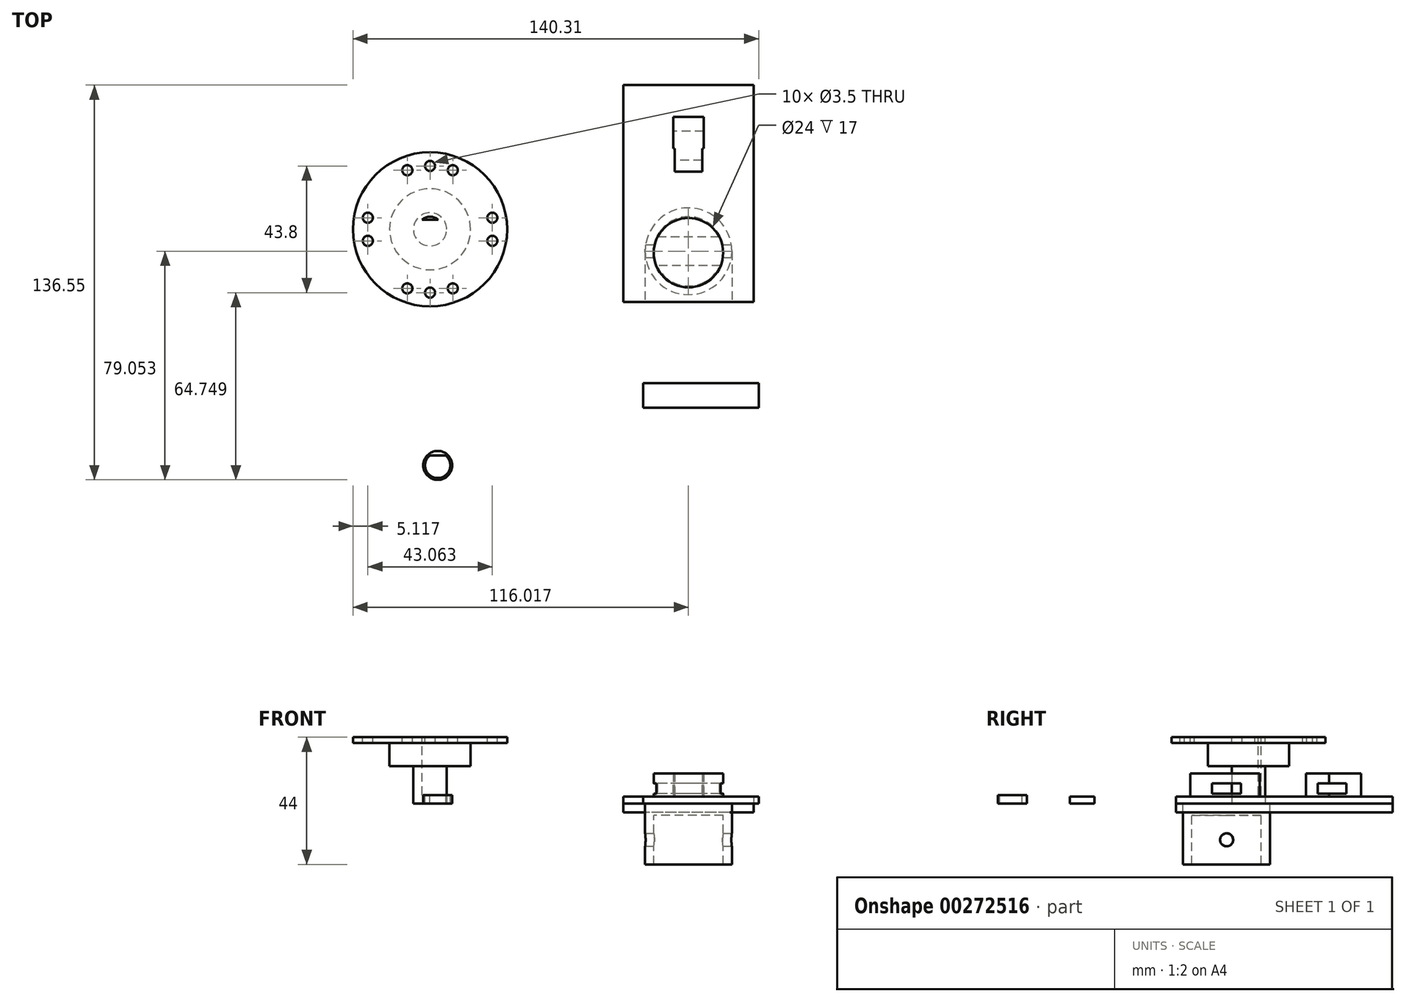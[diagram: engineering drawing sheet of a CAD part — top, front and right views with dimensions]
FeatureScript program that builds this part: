
annotation { "Feature Type Name" : "Feature", "Feature Type Description" : "" }
export const myFeature = defineFeature(function(context is Context, id is Id, definition is map)
    precondition{}
    {
        {
            var Q0;
            Q0=qCreatedBy(makeId("Top.planeOp"),FACE);
            var sketch = newSketch(context, id + "F0", { "sketchPlane" : qUnion([Q0])});
            skLineSegment(sketch, "E0.bottom", {"start": v(64.4, 9.3) * mm, "end": v(19.4, 9.3) * mm});
            skLineSegment(sketch, "E0.top", {"start": v(64.4, 84.3) * mm, "end": v(19.4, 84.3) * mm});
            skLineSegment(sketch, "E0.left", {"start": v(64.4, 9.3) * mm, "end": v(64.4, 84.3) * mm});
            skLineSegment(sketch, "E0.right", {"start": v(19.4, 9.3) * mm, "end": v(19.4, 84.3) * mm});
            skPoint(sketch, "E0.middle", {"position": v(41.9, 46.8) * mm});
            skSolve(sketch);
        }
        {
            var Q0;
            Q0=makeQuery(id+"F0.imprint","IMPRINT",FACE,{"disambiguationData":[TD([[makeQuery(id+"F0.imprint","IMPRINT",EDGE,{"derivedFrom":sQuery(id+"F0.wireOp",EDGE,"E0.bottom")}),-1.0]])]});
            extrude(context, id + "F1", {"entities" : qUnion([Q0]), "depth" : 2.5 * mm});
        }
        {
            var Q0;
            Q0=makeQuery(id+"F1.opExtrude","CAP_FACE",FACE,{"disambiguationData":[OSD([sQuery(id+"F0.wireOp",EDGE,"E0.bottom"),sQuery(id+"F0.wireOp",EDGE,"E0.top"),sQuery(id+"F0.wireOp",EDGE,"E0.left"),sQuery(id+"F0.wireOp",EDGE,"E0.right")])],"isStart":false});
            var sketch = newSketch(context, id + "F2", { "sketchPlane" : qUnion([Q0])});
            skCircle(sketch, "E1", {"center": v(41.9, 26.3) * mm, "radius": 12 * mm});
            skPoint(sketch, "E1.centerSnap0", {"position": v(41.9, 9.3) * mm});
            skPoint(sketch, "E2", {"position": v(41.9, 38.3) * mm});
            skLineSegment(sketch, "E3.bottom", {"start": v(46.65, 54.3) * mm, "end": v(37.15, 54.3) * mm});
            skLineSegment(sketch, "E3.top", {"start": v(46.65, 62.3) * mm, "end": v(37.15, 62.3) * mm});
            skLineSegment(sketch, "E3.left", {"start": v(46.65, 54.3) * mm, "end": v(46.65, 62.3) * mm});
            skLineSegment(sketch, "E3.right", {"start": v(37.15, 54.3) * mm, "end": v(37.15, 62.3) * mm});
            skPoint(sketch, "E3.middle", {"position": v(41.9, 58.3) * mm});
            skPoint(sketch, "E4", {"position": v(41.9, 54.3) * mm});
            skLineSegment(sketch, "E5.bottom", {"start": v(36.65, 62.3) * mm, "end": v(47.15, 62.3) * mm});
            skLineSegment(sketch, "E5.top", {"start": v(36.65, 73.3) * mm, "end": v(47.15, 73.3) * mm});
            skLineSegment(sketch, "E5.left", {"start": v(36.65, 62.3) * mm, "end": v(36.65, 73.3) * mm});
            skLineSegment(sketch, "E5.right", {"start": v(47.15, 62.3) * mm, "end": v(47.15, 73.3) * mm});
            skSolve(sketch);
        }
        {
            var Q0;
            Q0 = qSketchRegion(id + "F2", true);
            extrude(context, id + "F3", {"entities" : qUnion([Q0]), "operationType" : NewBodyOperationType.ADD, "depth" : 8 * mm});
        }
        {
            var Q0;
            Q0=makeQuery(id+"F0.imprint","IMPRINT",FACE,{"disambiguationData":[TD([[makeQuery(id+"F0.imprint","IMPRINT",EDGE,{"derivedFrom":sQuery(id+"F0.wireOp",EDGE,"E0.bottom")}),-1.0]])]});
            var sketch = newSketch(context, id + "F4", { "sketchPlane" : qUnion([Q0])});
            skPoint(sketch, "E6", {"position": v(41.9, 84.2) * mm});
            skPoint(sketch, "E7", {"position": v(41.9, 46.86) * mm});
            skLineSegment(sketch, "E8", {"start": v(41.9, 46.86) * mm, "end": v(41.9, 84.2) * mm});
            skCircle(sketch, "E9", {"center": v(41.9, 26.8) * mm, "radius": 15 * mm});
            skCircle(sketch, "E10", {"center": v(41.9, 26.8) * mm, "radius": 12 * mm});
            skSolve(sketch);
        }
        {
            var Q0;
            Q0=makeQuery(id+"F4.imprint","IMPRINT",FACE,{"disambiguationData":[TD([[makeQuery(id+"F4.imprint","IMPRINT",EDGE,{"derivedFrom":sQuery(id+"F4.wireOp",EDGE,"E9")}),1.0]])]});
            var Q1;
            Q1=makeQuery(id+"F4.imprint","IMPRINT",FACE,{"disambiguationData":[TD([[makeQuery(id+"F4.imprint","IMPRINT",EDGE,{"derivedFrom":sQuery(id+"F4.wireOp",EDGE,"E10")}),1.0]])]});
            extrude(context, id + "F5", {"entities" : qUnion([Q0, Q1]), "operationType" : NewBodyOperationType.ADD, "oppositeDirection" : true, "depth" : 4 * mm});
        }
        {
            var Q0;
            Q0 = qSketchRegion(id + "F4", true);
            extrude(context, id + "F6", {"entities" : qUnion([Q0]), "operationType" : NewBodyOperationType.ADD, "oppositeDirection" : true, "depth" : 21 * mm});
        }
        {
            var Q0;
            Q0=makeQuery(id+"F1.opExtrude","SWEPT_FACE",FACE,{"disambiguationData":[OSD([sQuery(id+"F0.wireOp",EDGE,"E0.bottom")])]});
            var sketch = newSketch(context, id + "F7", { "sketchPlane" : qUnion([Q0])});
            skLineSegment(sketch, "E11.bottom", {"start": v(62.65, -17.52) * mm, "end": v(21.14, -17.52) * mm});
            skLineSegment(sketch, "E11.top", {"start": v(62.65, 20.02) * mm, "end": v(21.14, 20.02) * mm});
            skLineSegment(sketch, "E11.left", {"start": v(62.65, -17.52) * mm, "end": v(62.65, 20.02) * mm});
            skLineSegment(sketch, "E11.right", {"start": v(21.14, -17.52) * mm, "end": v(21.14, 20.02) * mm});
            skPoint(sketch, "E11.middle", {"position": v(41.9, 1.25) * mm});
            skPoint(sketch, "E11.middle.positionSnap0", {"position": v(64.4, 1.25) * mm});
            skPoint(sketch, "E11.middle.positionSnap1", {"position": v(41.9, 2.5) * mm});
            skPoint(sketch, "E11.centerSnap0", {"position": v(64.4, 1.25) * mm});
            skPoint(sketch, "E11.centerSnap1", {"position": v(41.9, 2.5) * mm});
            skSolve(sketch);
        }
        {
            var Q0;
            Q0 = qSketchRegion(id + "F7", true);
            extrude(context, id + "F8", {"entities" : qUnion([Q0]), "operationType" : NewBodyOperationType.ADD, "depth" : 1 * mm});
        }
        {
            var Q0;
            Q0=makeQuery(id+"F8.opExtrude","CAP_FACE",FACE,{"disambiguationData":[OSD([sQuery(id+"F7.wireOp",EDGE,"E11.bottom"),sQuery(id+"F7.wireOp",EDGE,"E11.top"),sQuery(id+"F7.wireOp",EDGE,"E11.left"),sQuery(id+"F7.wireOp",EDGE,"E11.right")])],"isStart":false});
            var sketch = newSketch(context, id + "F9", { "sketchPlane" : qUnion([Q0])});
            skLineSegment(sketch, "E12.bottom", {"start": v(21.14, 20.02) * mm, "end": v(62.65, 20.02) * mm});
            skLineSegment(sketch, "E12.top", {"start": v(21.14, -17.52) * mm, "end": v(62.65, -17.52) * mm});
            skLineSegment(sketch, "E12.left", {"start": v(21.14, 20.02) * mm, "end": v(21.14, -17.52) * mm});
            skLineSegment(sketch, "E12.right", {"start": v(62.65, 20.02) * mm, "end": v(62.65, -17.52) * mm});
            skSolve(sketch);
        }
        {
            var Q0;
            Q0 = qSketchRegion(id + "F9", true);
            extrude(context, id + "F10", {"entities" : qUnion([Q0]), "operationType" : NewBodyOperationType.REMOVE, "oppositeDirection" : true, "depth" : 1 * mm});
        }
        {
            var Q0;
            Q0=makeQuery(id+"F1.opExtrude","SWEPT_FACE",FACE,{"disambiguationData":[OSD([sQuery(id+"F0.wireOp",EDGE,"E0.right")])]});
            var sketch = newSketch(context, id + "F11", { "sketchPlane" : qUnion([Q0])});
            skLineSegment(sketch, "E13.bottom", {"start": v(-84.3, 0) * mm, "end": v(-9.3, 0) * mm});
            skLineSegment(sketch, "E13.top", {"start": v(-84.3, 7.62) * mm, "end": v(-9.3, 7.62) * mm});
            skLineSegment(sketch, "E13.left", {"start": v(-84.3, 0) * mm, "end": v(-84.3, 7.62) * mm});
            skLineSegment(sketch, "E13.right", {"start": v(-9.3, 0) * mm, "end": v(-9.3, 7.62) * mm});
            skSolve(sketch);
        }
        {
            var Q0;
            Q0 = qSketchRegion(id + "F11", true);
            extrude(context, id + "F12", {"entities" : qUnion([Q0]), "operationType" : NewBodyOperationType.ADD, "depth" : 1 * mm});
        }
        {
            var Q0;
            Q0=makeQuery(id+"F12.opExtrude","CAP_FACE",FACE,{"disambiguationData":[OSD([sQuery(id+"F11.wireOp",EDGE,"E13.bottom"),sQuery(id+"F11.wireOp",EDGE,"E13.top"),sQuery(id+"F11.wireOp",EDGE,"E13.left"),sQuery(id+"F11.wireOp",EDGE,"E13.right")])],"isStart":false});
            var sketch = newSketch(context, id + "F13", { "sketchPlane" : qUnion([Q0])});
            skPoint(sketch, "E14", {"position": v(-26.8, 3.5) * mm});
            skLineSegment(sketch, "E15.bottom", {"start": v(-31.8, 3.5) * mm, "end": v(-21.8, 3.5) * mm});
            skLineSegment(sketch, "E15.top", {"start": v(-31.8, 7) * mm, "end": v(-21.8, 7) * mm});
            skLineSegment(sketch, "E15.left", {"start": v(-31.8, 3.5) * mm, "end": v(-31.8, 7) * mm});
            skLineSegment(sketch, "E15.right", {"start": v(-21.8, 3.5) * mm, "end": v(-21.8, 7) * mm});
            skLineSegment(sketch, "E16.bottom", {"start": v(-58.3, 3.5) * mm, "end": v(-68.3, 3.5) * mm});
            skLineSegment(sketch, "E16.top", {"start": v(-58.3, 7) * mm, "end": v(-68.3, 7) * mm});
            skLineSegment(sketch, "E16.left", {"start": v(-58.3, 3.5) * mm, "end": v(-58.3, 7) * mm});
            skLineSegment(sketch, "E16.right", {"start": v(-68.3, 3.5) * mm, "end": v(-68.3, 7) * mm});
            skPoint(sketch, "E17", {"position": v(-63.3, 5.25) * mm});
            skPoint(sketch, "E17.positionSnap0", {"position": v(-58.3, 5.25) * mm});
            skPoint(sketch, "E17.positionSnap1", {"position": v(-63.3, 3.5) * mm});
            skSolve(sketch);
        }
        {
            var Q0;
            Q0=makeQuery(id+"F13.imprint","IMPRINT",FACE,{"disambiguationData":[TD([[makeQuery(id+"F13.imprint","IMPRINT",EDGE,{"derivedFrom":sQuery(id+"F13.wireOp",EDGE,"E16.bottom")}),-1.0]])]});
            var Q1;
            Q1=makeQuery(id+"F13.imprint","IMPRINT",FACE,{"disambiguationData":[TD([[makeQuery(id+"F13.imprint","IMPRINT",EDGE,{"derivedFrom":sQuery(id+"F13.wireOp",EDGE,"E15.bottom")}),1.0]])]});
            extrude(context, id + "F14", {"entities" : qUnion([Q0, Q1]), "operationType" : NewBodyOperationType.REMOVE, "endBound" : BoundingType.THROUGH_ALL, "oppositeDirection" : true, "depth" : 25 * mm});
        }
        {
            var Q0;
            Q0=makeQuery(id+"F12.opExtrude","CAP_FACE",FACE,{"disambiguationData":[OSD([sQuery(id+"F11.wireOp",EDGE,"E13.bottom"),sQuery(id+"F11.wireOp",EDGE,"E13.top"),sQuery(id+"F11.wireOp",EDGE,"E13.left"),sQuery(id+"F11.wireOp",EDGE,"E13.right")])],"isStart":false});
            var sketch = newSketch(context, id + "F15", { "sketchPlane" : qUnion([Q0])});
            skLineSegment(sketch, "E18.bottom", {"start": v(-84.3, 7.62) * mm, "end": v(-9.3, 7.62) * mm});
            skLineSegment(sketch, "E18.top", {"start": v(-84.3, 0) * mm, "end": v(-9.3, 0) * mm});
            skLineSegment(sketch, "E18.left", {"start": v(-84.3, 7.62) * mm, "end": v(-84.3, 0) * mm});
            skLineSegment(sketch, "E18.right", {"start": v(-9.3, 7.62) * mm, "end": v(-9.3, 0) * mm});
            skSolve(sketch);
        }
        {
            var Q0;
            Q0 = qSketchRegion(id + "F15", true);
            extrude(context, id + "F16", {"entities" : qUnion([Q0]), "operationType" : NewBodyOperationType.REMOVE, "oppositeDirection" : true, "depth" : 1 * mm});
        }
        {
            var Q0;
            Q0=qCreatedBy(makeId("Top.planeOp"),FACE);
            var sketch = newSketch(context, id + "F17", { "sketchPlane" : qUnion([Q0])});
            skCircle(sketch, "E19", {"center": v(-47.47, 34.39) * mm, "radius": 5.75 * mm});
            skSolve(sketch);
        }
        {
            var Q0;
            Q0 = qSketchRegion(id + "F17", true);
            extrude(context, id + "F18", {"entities" : qUnion([Q0]), "depth" : 13 * mm});
        }
        {
            var Q0;
            Q0=makeQuery(id+"F18.opExtrude","CAP_FACE",FACE,{"disambiguationData":[OSD([sQuery(id+"F17.wireOp",EDGE,"E19")])],"isStart":false});
            var sketch = newSketch(context, id + "F19", { "sketchPlane" : qUnion([Q0])});
            skCircle(sketch, "E20", {"center": v(-47.47, 34.39) * mm, "radius": 14 * mm});
            skSolve(sketch);
        }
        {
            var Q0;
            Q0 = qSketchRegion(id + "F19", true);
            extrude(context, id + "F20", {"entities" : qUnion([Q0]), "operationType" : NewBodyOperationType.ADD, "depth" : 8 * mm});
        }
        {
            var Q0;
            Q0=makeQuery(id+"F20.opExtrude","CAP_FACE",FACE,{"disambiguationData":[OSD([sQuery(id+"F19.wireOp",EDGE,"E20")])],"isStart":false});
            var sketch = newSketch(context, id + "F21", { "sketchPlane" : qUnion([Q0])});
            skCircle(sketch, "E21", {"center": v(-47.47, 34.39) * mm, "radius": 26.65 * mm});
            skSolve(sketch);
        }
        {
            var Q0;
            Q0 = qSketchRegion(id + "F21", true);
            extrude(context, id + "F22", {"entities" : qUnion([Q0]), "operationType" : NewBodyOperationType.ADD, "depth" : 2 * mm});
        }
        {
            var Q0;
            Q0=makeQuery(id+"F22.opExtrude","CAP_FACE",FACE,{"disambiguationData":[OSD([sQuery(id+"F21.wireOp",EDGE,"E21")])],"isStart":false});
            var sketch = newSketch(context, id + "F23", { "sketchPlane" : qUnion([Q0])});
            skPoint(sketch, "E22", {"position": v(-47.47, 34.39) * mm});
            skPoint(sketch, "E23", {"position": v(-47.47, 61.04) * mm});
            skPoint(sketch, "E24", {"position": v(-47.47, 7.74) * mm});
            skPoint(sketch, "E25", {"position": v(-20.82, 34.39) * mm});
            skPoint(sketch, "E26", {"position": v(-74.12, 34.39) * mm});
            skCircle(sketch, "E27", {"center": v(-47.47, 56.29) * mm, "radius": 1.75 * mm});
            skCircle(sketch, "E28", {"center": v(-47.47, 12.49) * mm, "radius": 1.75 * mm});
            skCircle(sketch, "E29", {"center": v(-25.94, 38.39) * mm, "radius": 1.75 * mm});
            skCircle(sketch, "E30", {"center": v(-25.94, 30.39) * mm, "radius": 1.75 * mm});
            skCircle(sketch, "E31", {"center": v(-69, 30.39) * mm, "radius": 1.75 * mm});
            skCircle(sketch, "E32", {"center": v(-69, 38.39) * mm, "radius": 1.75 * mm});
            skPoint(sketch, "E33", {"position": v(-25.82, 34.39) * mm});
            skPoint(sketch, "E34", {"position": v(-69.12, 34.39) * mm});
            skCircle(sketch, "E35", {"center": v(-39.6, 54.83) * mm, "radius": 1.75 * mm});
            skCircle(sketch, "E36", {"center": v(-55.34, 54.83) * mm, "radius": 1.75 * mm});
            skCircle(sketch, "E37", {"center": v(-39.6, 13.95) * mm, "radius": 1.75 * mm});
            skCircle(sketch, "E38", {"center": v(-55.34, 13.95) * mm, "radius": 1.75 * mm});
            skSolve(sketch);
        }
        {
            var Q0;
            Q0 = qSketchRegion(id + "F23", true);
            extrude(context, id + "F24", {"entities" : qUnion([Q0]), "operationType" : NewBodyOperationType.REMOVE, "oppositeDirection" : true, "depth" : 25 * mm});
        }
        {
            var Q0;
            Q0=makeQuery(id+"F22.opExtrude","CAP_FACE",FACE,{"disambiguationData":[OSD([sQuery(id+"F21.wireOp",EDGE,"E21")])],"isStart":false});
            var sketch = newSketch(context, id + "F25", { "sketchPlane" : qUnion([Q0])});
            skCircle(sketch, "E39", {"center": v(-47.47, 34.39) * mm, "radius": 4.38 * mm});
            skPoint(sketch, "E40", {"position": v(-47.47, 37.76) * mm});
            skLineSegment(sketch, "E41.bottom", {"start": v(-51.18, 37.76) * mm, "end": v(-44.58, 37.76) * mm});
            skLineSegment(sketch, "E41.top", {"start": v(-51.18, 39.65) * mm, "end": v(-44.58, 39.65) * mm});
            skLineSegment(sketch, "E41.left", {"start": v(-51.18, 37.76) * mm, "end": v(-51.18, 39.65) * mm});
            skLineSegment(sketch, "E41.right", {"start": v(-44.58, 37.76) * mm, "end": v(-44.58, 39.65) * mm});
            skSolve(sketch);
        }
        {
            var Q0;
            {var subQ0=sQuery(id+"F25.wireOp",EDGE,"E41.bottom");var subQ1=sQuery(id+"F25.wireOp",EDGE,"E39");var subQ2=makeQuery(id+"F25.imprint","INTERSECT",VERTEX,{"disambiguationData":[OD(0.0)],"derivedFrom":[subQ1,subQ0]});Q0=makeQuery(id+"F25.imprint","IMPRINT",FACE,{"disambiguationData":[TD([[makeQuery(id+"F25.imprint","IMPRINT",EDGE,{"disambiguationData":[TD([[subQ2,-1.0]])],"derivedFrom":subQ1}),1.0]])]});}
            extrude(context, id + "F26", {"entities" : qUnion([Q0]), "operationType" : NewBodyOperationType.REMOVE, "oppositeDirection" : true, "depth" : 20 * mm});
        }
        {
            var Q0;
            Q0=qCreatedBy(makeId("Top.planeOp"),FACE);
            var sketch = newSketch(context, id + "F27", { "sketchPlane" : qUnion([Q0])});
            skLineSegment(sketch, "E42.bottom", {"start": v(26.19, -27.32) * mm, "end": v(66.19, -27.32) * mm});
            skLineSegment(sketch, "E42.top", {"start": v(26.19, -18.82) * mm, "end": v(66.19, -18.82) * mm});
            skLineSegment(sketch, "E42.left", {"start": v(26.19, -27.32) * mm, "end": v(26.19, -18.82) * mm});
            skLineSegment(sketch, "E42.right", {"start": v(66.19, -27.32) * mm, "end": v(66.19, -18.82) * mm});
            skSolve(sketch);
        }
        {
            var Q0;
            Q0 = qSketchRegion(id + "F27", true);
            extrude(context, id + "F28", {"entities" : qUnion([Q0]), "depth" : 2.5 * mm});
        }
        {
            var Q0;
            Q0=qCreatedBy(makeId("Top.planeOp"),FACE);
            var sketch = newSketch(context, id + "F29", { "sketchPlane" : qUnion([Q0])});
            skCircle(sketch, "E43", {"center": v(-44.83, -47.26) * mm, "radius": 5 * mm});
            skSolve(sketch);
        }
        {
            var Q0;
            Q0 = qSketchRegion(id + "F29", true);
            extrude(context, id + "F30", {"entities" : qUnion([Q0]), "depth" : 3 * mm});
        }
        {
            var Q0;
            Q0=makeQuery(id+"F30.opExtrude","CAP_FACE",FACE,{"disambiguationData":[OSD([sQuery(id+"F29.wireOp",EDGE,"E43")])],"isStart":false});
            var sketch = newSketch(context, id + "F31", { "sketchPlane" : qUnion([Q0])});
            skCircle(sketch, "E44", {"center": v(-44.83, -47.26) * mm, "radius": 4.38 * mm});
            skPoint(sketch, "E45", {"position": v(-44.83, -43.89) * mm});
            skLineSegment(sketch, "E46.bottom", {"start": v(-51.07, -43.89) * mm, "end": v(-39.01, -43.89) * mm});
            skLineSegment(sketch, "E46.top", {"start": v(-51.07, -41.6) * mm, "end": v(-39.01, -41.6) * mm});
            skLineSegment(sketch, "E46.left", {"start": v(-51.07, -43.89) * mm, "end": v(-51.07, -41.6) * mm});
            skLineSegment(sketch, "E46.right", {"start": v(-39.01, -43.89) * mm, "end": v(-39.01, -41.6) * mm});
            skSolve(sketch);
        }
        {
            var Q0;
            {var subQ0=sQuery(id+"F31.wireOp",EDGE,"E46.bottom");var subQ1=sQuery(id+"F31.wireOp",EDGE,"E44");var subQ2=makeQuery(id+"F31.imprint","INTERSECT",VERTEX,{"disambiguationData":[OD(0.0)],"derivedFrom":[subQ1,subQ0]});Q0=makeQuery(id+"F31.imprint","IMPRINT",FACE,{"disambiguationData":[TD([[makeQuery(id+"F31.imprint","IMPRINT",EDGE,{"disambiguationData":[TD([[subQ2,-1.0]])],"derivedFrom":subQ1}),1.0]])]});}
            extrude(context, id + "F32", {"entities" : qUnion([Q0]), "operationType" : NewBodyOperationType.REMOVE, "oppositeDirection" : true, "depth" : 25 * mm});
        }
        {
            var Q0;
            Q0=makeQuery(id+"F1.opExtrude","SWEPT_FACE",FACE,{"disambiguationData":[OSD([sQuery(id+"F0.wireOp",EDGE,"E0.left")])]});
            var sketch = newSketch(context, id + "F33", { "sketchPlane" : qUnion([Q0])});
            skPoint(sketch, "E47", {"position": v(26.84, 1.25) * mm});
            skPoint(sketch, "E47.positionSnap0", {"position": v(9.3, 1.25) * mm});
            skPoint(sketch, "E48", {"position": v(26.84, 2.5) * mm});
            skCircle(sketch, "E49", {"center": v(26.84, -12.5) * mm, "radius": 2.25 * mm});
            skSolve(sketch);
        }
        {
            var Q0;
            Q0=makeQuery(id+"F33.imprint","IMPRINT",FACE,{"disambiguationData":[TD([[makeQuery(id+"F33.imprint","IMPRINT",EDGE,{"derivedFrom":sQuery(id+"F33.wireOp",EDGE,"E49")}),1.0]])]});
            extrude(context, id + "F34", {"entities" : qUnion([Q0]), "operationType" : NewBodyOperationType.REMOVE, "oppositeDirection" : true, "depth" : 58.7 * mm});
        }
        {
            var Q0;
            Q0=makeQuery(id+"F0.imprint","IMPRINT",FACE,{"disambiguationData":[TD([[makeQuery(id+"F0.imprint","IMPRINT",EDGE,{"derivedFrom":sQuery(id+"F0.wireOp",EDGE,"E0.bottom")}),-1.0]])]});
            extrude(context, id + "F35", {"entities" : qUnion([Q0]), "operationType" : NewBodyOperationType.ADD, "oppositeDirection" : true, "depth" : 0 * mm});
        }
        {
            var Q0;
            Q0=makeQuery(id+"F35.opExtrude","CAP_FACE",FACE,{"disambiguationData":[OSD([sQuery(id+"F0.wireOp",EDGE,"E0.bottom"),sQuery(id+"F0.wireOp",EDGE,"E0.top"),sQuery(id+"F0.wireOp",EDGE,"E0.left"),sQuery(id+"F0.wireOp",EDGE,"E0.right")])],"isStart":false});
            var sketch = newSketch(context, id + "F36", { "sketchPlane" : qUnion([Q0])});
            skLineSegment(sketch, "E50.bottom", {"start": v(19.4, -84.3) * mm, "end": v(64.4, -84.3) * mm});
            skLineSegment(sketch, "E50.top", {"start": v(19.4, -9.3) * mm, "end": v(64.4, -9.3) * mm});
            skLineSegment(sketch, "E50.left", {"start": v(19.4, -84.3) * mm, "end": v(19.4, -9.3) * mm});
            skLineSegment(sketch, "E50.right", {"start": v(64.4, -84.3) * mm, "end": v(64.4, -9.3) * mm});
            skCircle(sketch, "E51", {"center": v(41.9, -26.8) * mm, "radius": 15 * mm});
            skLineSegment(sketch, "E52.bottom", {"start": v(26.9, -26.8) * mm, "end": v(56.9, -26.8) * mm});
            skLineSegment(sketch, "E52.top", {"start": v(26.9, -9.3) * mm, "end": v(56.9, -9.3) * mm});
            skLineSegment(sketch, "E52.left", {"start": v(26.9, -26.8) * mm, "end": v(26.9, -9.3) * mm});
            skLineSegment(sketch, "E52.right", {"start": v(56.9, -26.8) * mm, "end": v(56.9, -9.3) * mm});
            skSolve(sketch);
        }
        {
            var Q0;
            Q0=makeQuery(id+"F36.imprint","IMPRINT",FACE,{"disambiguationData":[TD([[makeQuery(id+"F36.imprint","IMPRINT",EDGE,{"derivedFrom":sQuery(id+"F36.wireOp",EDGE,"E50.bottom")}),-1.0]])]});
            extrude(context, id + "F37", {"entities" : qUnion([Q0]), "depth" : 3 * mm});
        }
    });
